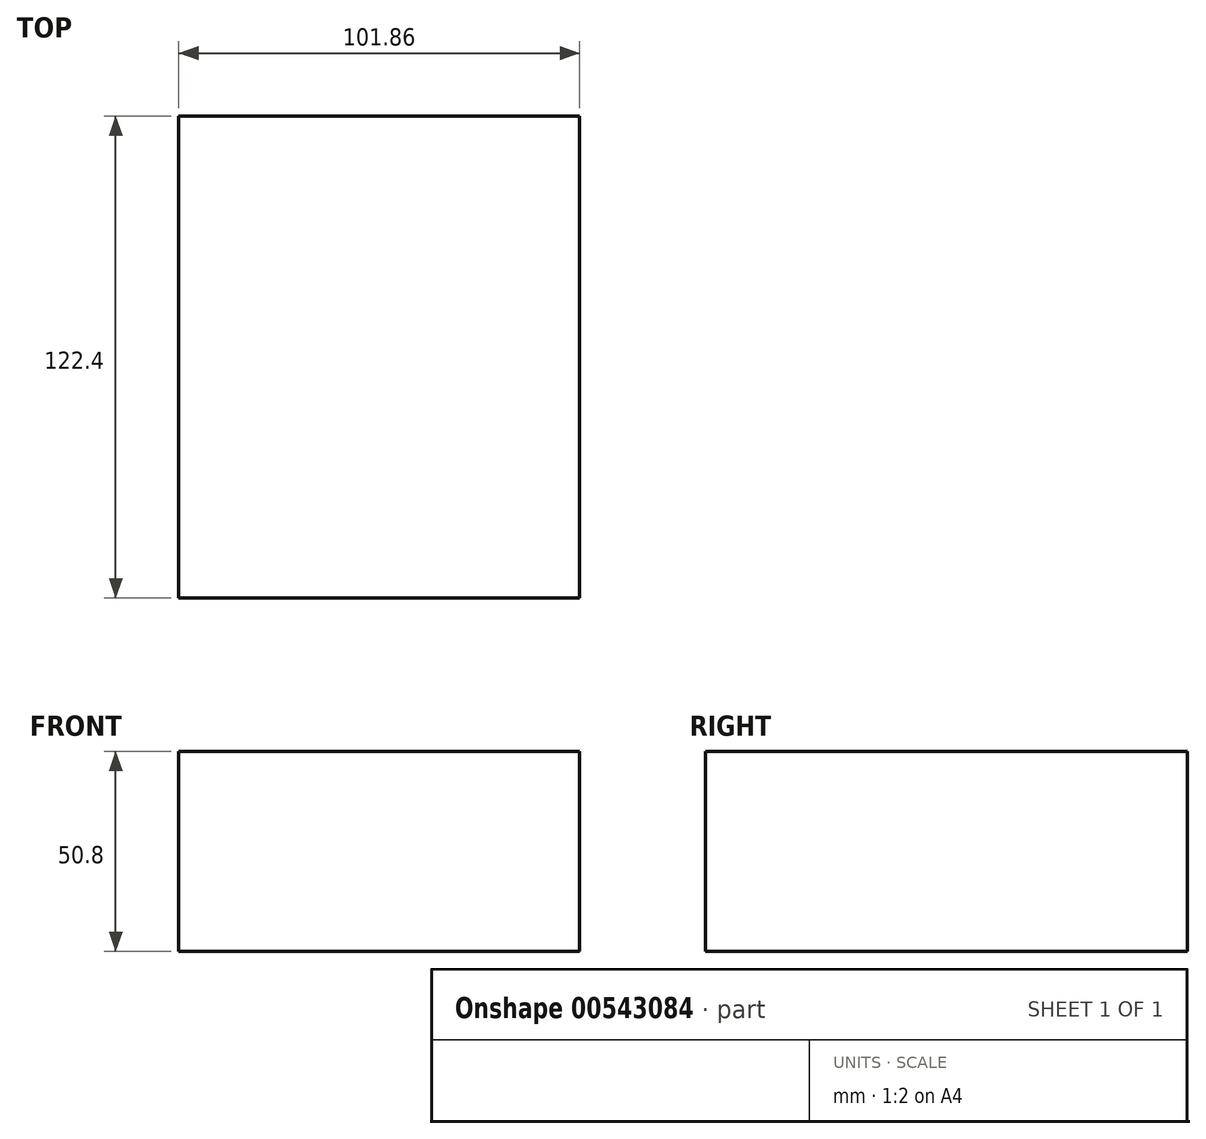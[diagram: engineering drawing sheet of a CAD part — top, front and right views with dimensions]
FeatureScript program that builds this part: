
annotation { "Feature Type Name" : "Feature", "Feature Type Description" : "" }
export const myFeature = defineFeature(function(context is Context, id is Id, definition is map)
    precondition{}
    {
        {
            var Q0;
            Q0=qCreatedBy(makeId("Top.planeOp"),FACE);
            var sketch = newSketch(context, id + "F0", { "sketchPlane" : qUnion([Q0])});
            skLineSegment(sketch, "E0.bottom", {"start": v(50.93, 61.2) * mm, "end": v(-50.93, 61.2) * mm});
            skLineSegment(sketch, "E0.top", {"start": v(50.93, -61.2) * mm, "end": v(-50.93, -61.2) * mm});
            skLineSegment(sketch, "E0.left", {"start": v(50.93, 61.2) * mm, "end": v(50.93, -61.2) * mm});
            skLineSegment(sketch, "E0.right", {"start": v(-50.93, 61.2) * mm, "end": v(-50.93, -61.2) * mm});
            skPoint(sketch, "E0.middle", {"position": v(0, 0) * mm});
            skSolve(sketch);
        }
        {
            var Q0;
            Q0 = qSketchRegion(id + "F0", true);
            extrude(context, id + "F1", {"entities" : qUnion([Q0]), "depth" : 50.8 * mm, "offsetDistance" : 25.4 * mm});
        }
    });
